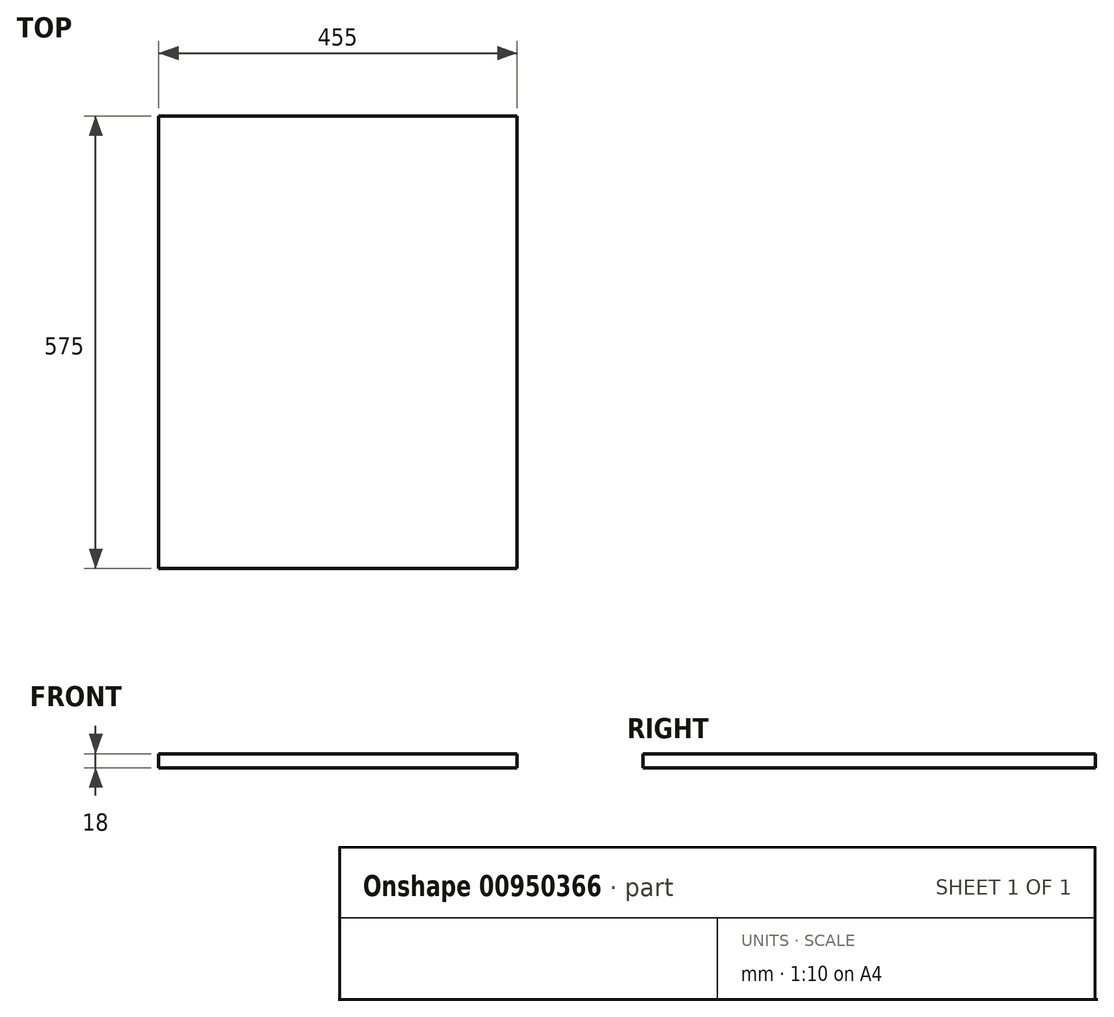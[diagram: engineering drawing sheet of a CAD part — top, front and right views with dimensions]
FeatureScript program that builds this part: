
annotation { "Feature Type Name" : "Feature", "Feature Type Description" : "" }
export const myFeature = defineFeature(function(context is Context, id is Id, definition is map)
    precondition{}
    {
        {
            var Q0;
            Q0=qCreatedBy(makeId("Top.planeOp"),FACE);
            var sketch = newSketch(context, id + "F0", { "sketchPlane" : qUnion([Q0])});
            skLineSegment(sketch, "E0.bottom", {"start": v(0, 513.38) * mm, "end": v(455, 513.38) * mm});
            skLineSegment(sketch, "E0.top", {"start": v(0, -61.62) * mm, "end": v(455, -61.62) * mm});
            skLineSegment(sketch, "E0.left", {"start": v(0, -61.62) * mm, "end": v(0, 513.38) * mm});
            skLineSegment(sketch, "E0.right", {"start": v(455, -61.62) * mm, "end": v(455, 513.38) * mm});
            skSolve(sketch);
        }
        {
            var Q0;
            Q0=makeQuery(id+"F0.imprint","IMPRINT",FACE,{"disambiguationData":[TD([[makeQuery(id+"F0.imprint","IMPRINT",EDGE,{"derivedFrom":sQuery(id+"F0.wireOp",EDGE,"E0.bottom")}),-1.0]])]});
            extrude(context, id + "F1", {"entities" : qUnion([Q0]), "depth" : 18 * mm, "offsetDistance" : 25 * mm});
        }
    });
